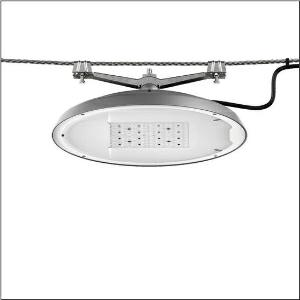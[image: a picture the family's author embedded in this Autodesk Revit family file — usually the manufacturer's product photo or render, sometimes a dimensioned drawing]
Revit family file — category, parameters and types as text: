
# Revit family: dl_r__50_iq_mini___st1_0s_5xa248w21f08me_4099
name_source: partatom
category: Lighting Fixtures
units: mm (PartAtom-declared; Revit-internal decimal feet)

## family parameters
Cut with Voids When Loaded = No
Host = Face
Light Source = No
Part Type = Normal
Room Calculation Point = No
Round Connector Dimension = Use Diameter
Shared = No

## types (1)
- --- (1 x LED, 12600 lm, 103.8 W, 2200K)
    Apparent Load = 104 VA
    CIE Flux Codes = 37 72 97 100 100
    Color Rendering = 70
    Color Temperature = 2200K
    Default Elevation = 1800 mm
    Description = DL® 50 iQ mini, catenary luminaire, primary light control with lens, of PMMA, primary optical cover: cover, of toughened safety glass, transparent, light distribution: ST1.0s, light emission: direct distribution, primary light characteristic: symmetric, installation type: suspended mounting, LED, High Power LED, rated luminous flux: 12.600lm, luminous efficacy: 121lm/W, light colour: 722, colour temperature: 2200K, control: optimised constant luminous flux control (CLO 2.0), Desk-Remote (wireless, voltage-free reading and setting of iQ features in the workshop via application-optimized NFC function/RFID function), Light-Fading, Smart-Wire, Night-Set, Lumen-Switch, Temp-Guard, Auto-Match, Street-Remote, mains connection: 230..240V, AC, 50/60Hz, start of lifetime: 104W, end of service life: 114W, reduction: 46W, luminaire housing, of diecast aluminium, powder-coated, Siteco® metallic grey (DB 702S), diameter: 500mm, height: 115mm, protection rating (complete): IP66, insulation class (complete): insulation class II (safety insulation), certification: CE, ENEC, VDE, impact resistance: IK08, permissible operating ambient temperature for outdoor applications: -25..+40°C, standard-compliant lighting for roads and squares, packaging unit: 1 piece

Light Distribution: ST1.0s
    Height = 124 mm  [stored 0.406824 ft]
    Lamp = 1 x LED
    Lamp Light Flux = 12600 lm
    Lamp Power = 103.8 W
    Lamp count = 1
    Length = 500 mm
    Luminous efficacy = 121 lm/W
    Manufacturer = Siteco
    ModVariant = No
    Model = 5XA248W21F08ME
    Number of Poles = 1
    OnlyDefault = Yes
    Power Factor = 1
    Product Name = DL® 50 iQ mini | ST1.0s
    Product group = catenary luminaire
    ProductGroupID = 6300
    Protection Class = Protection class II
    Protection Degree = IP 66
    RLX_Detail_Level = 1
    RLX_Emergency_Light_Flux = 0 lm
    RLX_Emergency_Type = 0
    RLX_Emergency_Type_DB = No
    RlxData = <blob elided: 127005 chars, md5=e6a46c4d>
    Socket = socket
    Standby Power = 0 W
    System Light Flux = 12600 lm
    System Power = 104 W
    Type Comments = factory setting: luminous flux: 100 % | dim-lin: 254 | 545 mA
    Type Image = l_1251783.jpg
    URL = http://relux.com
    VarID = @adj_089819
    Voltage = 0 V
    Weight = 0.00 kg
    Width = 0 mm  [stored 0 ft]

note: [stored X ft] marks values corroborated as IEEE doubles in the binary element streams (Revit-internal decimal feet)

## geometry (parser evidence)
native form markers: Blend x4, Sweep x15
no freeform markers — native parametric forms only
